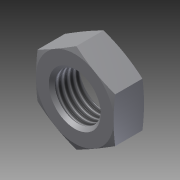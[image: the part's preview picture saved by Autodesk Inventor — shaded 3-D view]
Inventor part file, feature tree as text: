
AUTODESK INVENTOR PART (.ipt)
format: ipt  version: 2012 (Build 160160000, 160)  size: 148,992 bytes
history: native  units: in
note: dims shown in document units (in); Inventor stores cm internally (conversion verified against a paired STEP export)
features: other x70, sketch x3, revolve x2, extrude x1, thread x1
ambient origin geometry x8: Origin, YZ Plane, XZ Plane, XY Plane, X Axis, Y Axis, Z Axis, Center Point
bodies: Solid1 (feature_tree)
feature tree (77):
  sketch  "Sketch_8"  dims[d0=360.0deg d1=0.22in d2=0.0in]
  sketch  "Sketch_10"  dims[d3=360.0deg d4=0.1749in d5=0.0in]
  revolve  "Revolution1"  [1 undecoded]
  extrude  "Extrusion1"  Depth=0.1749in TaperAngle=0.0deg
  revolve  "Revolution2"  [1 undecoded]
  thread  "Thread1"  [1 undecoded]
  other  "NUT_XY"
  other  "NUT_YZ"
  other  "NUT_ZX"
  other  "NUT_X"
  other  "NUT_Y"
  other  "NUT_Z"
  other  "NUT_Center"
  other  "a1_XY"
  other  "a1_YZ"
  other  "a1_ZX"
  other  "a1_X"
  other  "a1_Y"
  other  "a1_Z"
  other  "a1_Center"
  other  "a2_XY"
  other  "a2_YZ"
  other  "a2_ZX"
  other  "a2_X"
  other  "a2_Y"
  other  "a2_Z"
  other  "a2_Center"
  other  "b1_XY"
  other  "b1_YZ"
  other  "b1_ZX"
  other  "b1_X"
  other  "b1_Y"
  other  "b1_Z"
  other  "b1_Center"
  other  "b2_XY"
  other  "b2_YZ"
  other  "b2_ZX"
  other  "b2_X"
  other  "b2_Y"
  other  "b2_Z"
  other  "b2_Center"
  other  "e_XY"
  other  "e_YZ"
  other  "e_ZX"
  other  "e_X"
  other  "e_Y"
  other  "e_Z"
  other  "e_Center"
  other  "th1_XY"
  other  "th1_YZ"
  other  "th1_ZX"
  other  "th1_X"
  other  "th1_Y"
  other  "th1_Z"
  other  "th1_Center"
  other  "th2_XY"
  other  "th2_YZ"
  other  "th2_ZX"
  other  "th2_X"
  other  "th2_Y"
  other  "th2_Z"
  other  "th2_Center"
  other  "ol1_XY"
  other  "ol1_YZ"
  other  "ol1_ZX"
  other  "ol1_X"
  other  "ol1_Y"
  other  "ol1_Z"
  other  "ol1_Center"
  other  "ol2_XY"
  other  "ol2_YZ"
  other  "ol2_ZX"
  other  "ol2_X"
  other  "ol2_Y"
  other  "ol2_Z"
  other  "ol2_Center"
  sketch  "Sketch_11"
note: 3 required parameter values undecoded (feature->parameter linkage not recoverable at this tier; creation-order binding heuristic only, values carry confidence <= 0.55)